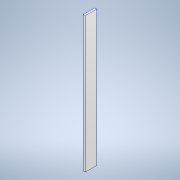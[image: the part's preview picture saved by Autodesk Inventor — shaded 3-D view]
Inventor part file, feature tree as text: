
AUTODESK INVENTOR PART (.ipt)
format: ipt  version: 2022 (Build 260153000, 153)  size: 95,232 bytes
history: native  units: mm
features: extrude x1, sketch x1
ambient origin geometry x8: Origin, YZ Plane, XZ Plane, XY Plane, X Axis, Y Axis, Z Axis, Center Point
bodies: Solid1 (feature_tree)
feature tree (2):
  extrude  "Extrusion1"  Depth=60.0mm
  sketch  "Sketch1"  dims[d0=10.0mm d1=60.0mm d2=700.0mm d3=0.0mm]
